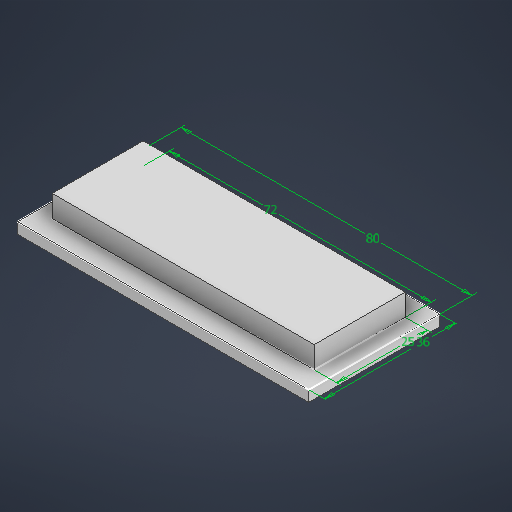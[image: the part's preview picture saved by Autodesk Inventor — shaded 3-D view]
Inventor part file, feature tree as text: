
AUTODESK INVENTOR PART (.ipt)
format: ipt  version: 2025.2 (Build 292293000, 293)  size: 194,048 bytes
history: native  units: mm
features: extrude x2, sketch x1
ambient origin geometry x8: Origin, YZ Plane, XZ Plane, XY Plane, X Axis, Y Axis, Z Axis, Center Point
bodies: Solid1 (feature_tree)
feature tree (3):
  sketch  "Sketch1"  dims[d0=36.0mm d1=80.0mm d2=25.0mm d3=72.0mm d4=3.0mm d5=0.0mm d6=6.0mm d7=0.0mm]
  extrude  "Extrusion1"  Depth=80.0mm
  extrude  "Extrusion2"  Depth=25.0mm
